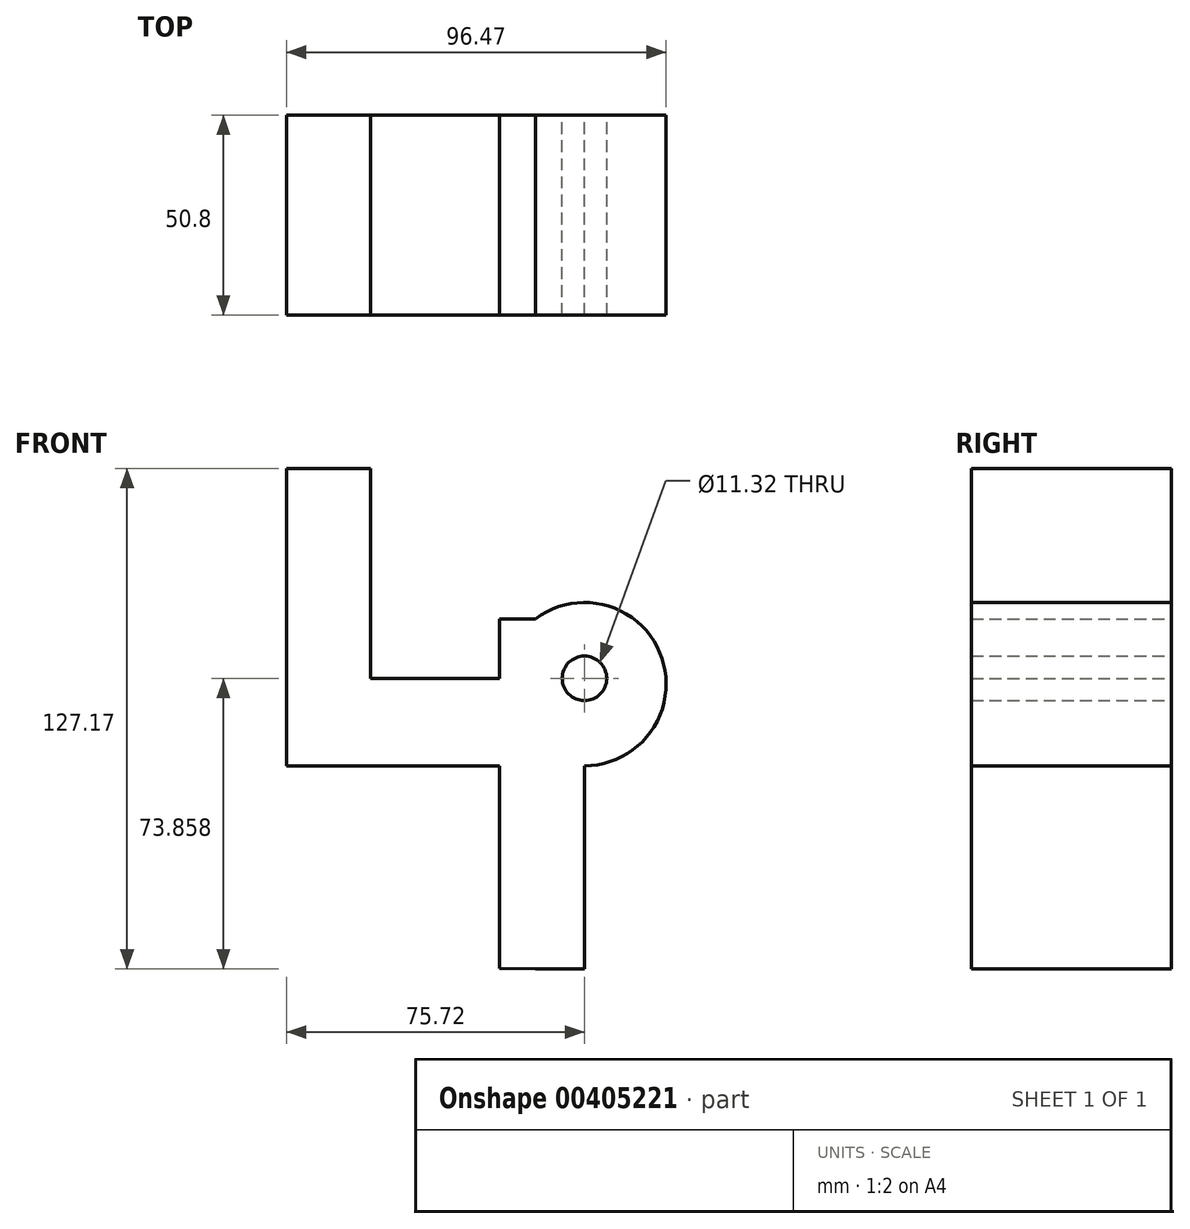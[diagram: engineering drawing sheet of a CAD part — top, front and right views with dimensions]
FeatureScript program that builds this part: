
annotation { "Feature Type Name" : "Feature", "Feature Type Description" : "" }
export const myFeature = defineFeature(function(context is Context, id is Id, definition is map)
    precondition{}
    {
        {
            var Q0;
            Q0=qCreatedBy(makeId("Front.planeOp"),FACE);
            var sketch = newSketch(context, id + "F0", { "sketchPlane" : qUnion([Q0])});
            skLineSegment(sketch, "E0.bottom", {"start": v(-75.72, 75.51) * mm, "end": v(-54.35, 75.51) * mm});
            skLineSegment(sketch, "E0.top", {"start": v(-75.72, 0) * mm, "end": v(-54.35, 0) * mm});
            skLineSegment(sketch, "E0.left", {"start": v(-75.72, 75.51) * mm, "end": v(-75.72, 0) * mm});
            skLineSegment(sketch, "E0.right", {"start": v(-54.35, 75.51) * mm, "end": v(-54.35, 0) * mm});
            skLineSegment(sketch, "E1.bottom", {"start": v(-54.35, 0) * mm, "end": v(0, 0) * mm});
            skLineSegment(sketch, "E1.top", {"start": v(-54.35, 22.2) * mm, "end": v(0, 22.2) * mm});
            skLineSegment(sketch, "E1.left", {"start": v(-54.35, 0) * mm, "end": v(-54.35, 22.2) * mm});
            skLineSegment(sketch, "E1.right", {"start": v(0, 0) * mm, "end": v(0, 22.2) * mm});
            skArc(sketch, "E2", {"start": v(0, 0) * mm, "mid": v(19.68, 27.3) * mm, "end": v(-12.45, 37.34) * mm});
            skCircle(sketch, "E3", {"center": v(0, 22.2) * mm, "radius": 5.66 * mm});
            skLineSegment(sketch, "E4", {"start": v(-12.45, 37.34) * mm, "end": v(-12.45, -51.66) * mm});
            skLineSegment(sketch, "E5", {"start": v(-12.45, -51.66) * mm, "end": v(0, -51.66) * mm});
            skPoint(sketch, "E5.endSnap0", {"position": v(0, 11.1) * mm});
            skLineSegment(sketch, "E6", {"start": v(-12.45, 37.34) * mm, "end": v(-21.58, 37.34) * mm});
            skLineSegment(sketch, "E7", {"start": v(-21.58, 37.34) * mm, "end": v(-21.58, -51.45) * mm});
            skLineSegment(sketch, "E8", {"start": v(-21.58, -51.45) * mm, "end": v(-12.45, -51.66) * mm});
            skLineSegment(sketch, "E9", {"start": v(0, -51.66) * mm, "end": v(0, 0) * mm});
            skSolve(sketch);
        }
        {
            var Q0;
            Q0 = qSketchRegion(id + "F0", true);
            extrude(context, id + "F1", {"entities" : qUnion([Q0]), "depth" : 50.8 * mm});
        }
    });
